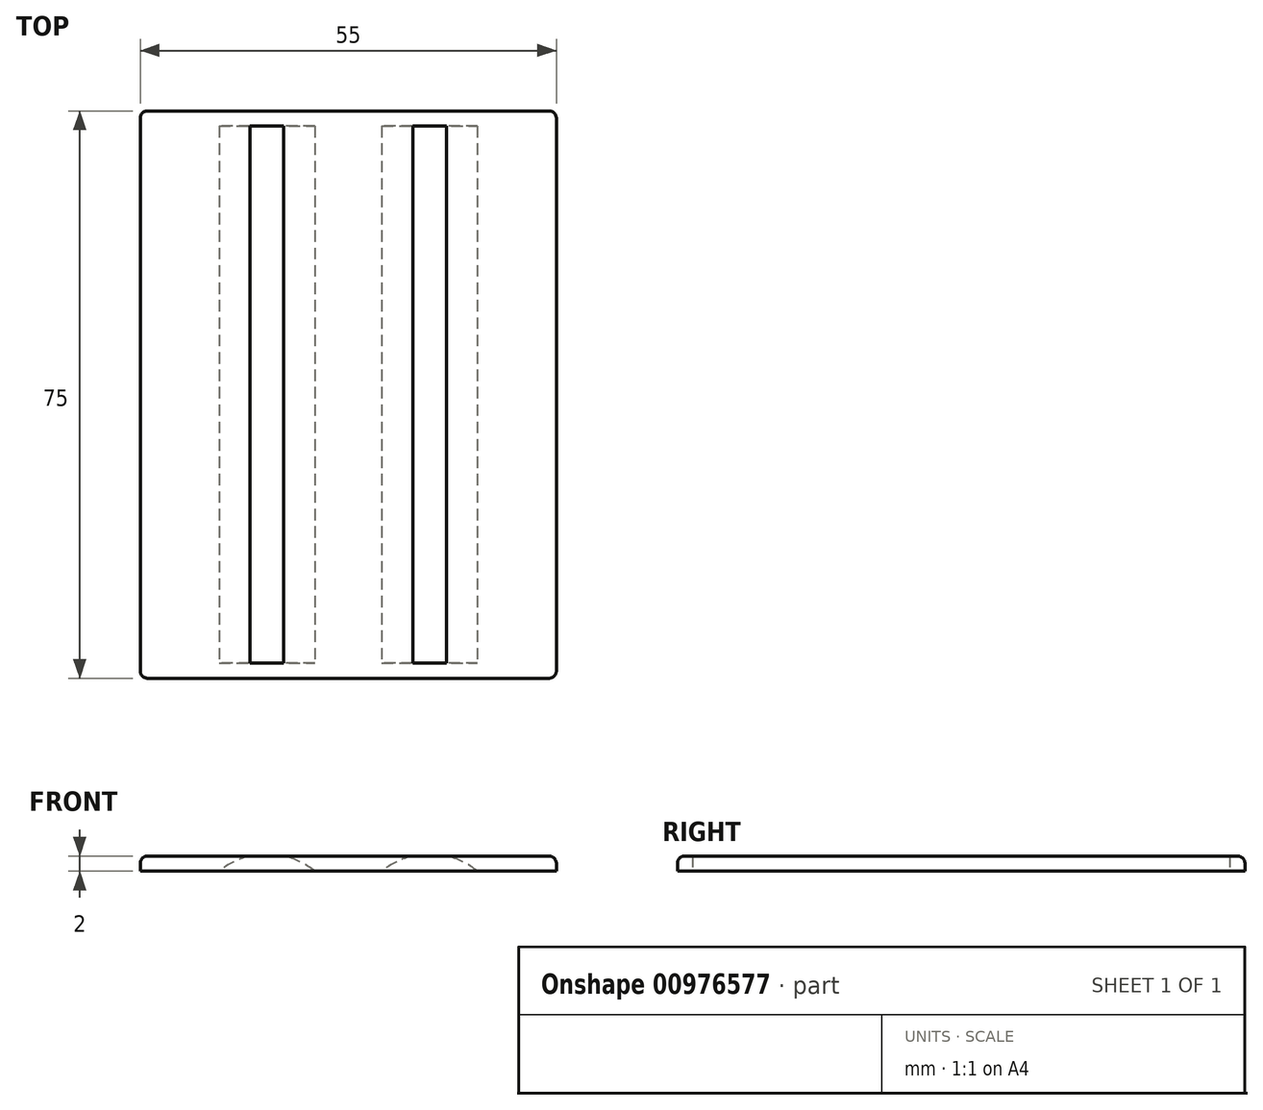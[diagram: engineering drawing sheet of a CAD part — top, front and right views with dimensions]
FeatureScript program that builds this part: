
annotation { "Feature Type Name" : "Feature", "Feature Type Description" : "" }
export const myFeature = defineFeature(function(context is Context, id is Id, definition is map)
    precondition{}
    {
        {
            var Q0;
            Q0=qCreatedBy(makeId("Top.planeOp"),FACE);
            var sketch = newSketch(context, id + "F0", { "sketchPlane" : qUnion([Q0])});
            skLineSegment(sketch, "E0.bottom", {"start": v(0, 0) * mm, "end": v(55, 0) * mm});
            skLineSegment(sketch, "E0.top", {"start": v(0, 73) * mm, "end": v(55, 73) * mm});
            skLineSegment(sketch, "E0.left", {"start": v(0, 0) * mm, "end": v(0, 73) * mm});
            skLineSegment(sketch, "E0.right", {"start": v(55, 0) * mm, "end": v(55, 73) * mm});
            skSolve(sketch);
        }
        {
            var Q0;
            Q0=makeQuery(id+"F0.imprint","IMPRINT",FACE,{"disambiguationData":[TD([[makeQuery(id+"F0.imprint","IMPRINT",EDGE,{"derivedFrom":sQuery(id+"F0.wireOp",EDGE,"E0.bottom")}),1.0]])]});
            extrude(context, id + "F1", {"entities" : qUnion([Q0]), "depth" : 2 * mm, "offsetDistance" : 25 * mm});
        }
        {
            var Q0;
            Q0=makeQuery(id+"F1.opExtrude","SWEPT_FACE",FACE,{"disambiguationData":[OSD([sQuery(id+"F0.wireOp",EDGE,"E0.bottom")])]});
            var sketch = newSketch(context, id + "F2", { "sketchPlane" : qUnion([Q0])});
            skCircle(sketch, "E1", {"center": v(16.75, -7.75) * mm, "radius": 10 * mm});
            skCircle(sketch, "E2", {"center": v(38.25, -7.75) * mm, "radius": 10 * mm});
            skSolve(sketch);
        }
        {
            var Q0;
            {var subQ0=sQuery(id+"F2.wireOp",EDGE,"E2");var subQ1=sQuery(id+"F0.wireOp",EDGE,"E0.bottom");var subQ2=makeQuery(id+"F1.opExtrude","CAP_EDGE",EDGE,{"disambiguationData":[OSD([subQ1])],"isStart":false});var subQ3=makeQuery(id+"F2.imprint","INTERSECT",VERTEX,{"disambiguationData":[OD(0.0)],"derivedFrom":[subQ2,subQ0]});Q0=makeQuery(id+"F2.imprint","IMPRINT",FACE,{"disambiguationData":[TD([[makeQuery(id+"F2.imprint","IMPRINT",EDGE,{"disambiguationData":[TD([[subQ3,1.0]])],"derivedFrom":subQ0}),1.0]])]});}
            var Q1;
            {var subQ0=sQuery(id+"F2.wireOp",EDGE,"E1");var subQ1=sQuery(id+"F0.wireOp",EDGE,"E0.bottom");var subQ2=makeQuery(id+"F1.opExtrude","CAP_EDGE",EDGE,{"disambiguationData":[OSD([subQ1])],"isStart":false});var subQ3=makeQuery(id+"F2.imprint","INTERSECT",VERTEX,{"disambiguationData":[OD(0.0)],"derivedFrom":[subQ2,subQ0]});Q1=makeQuery(id+"F2.imprint","IMPRINT",FACE,{"disambiguationData":[TD([[makeQuery(id+"F2.imprint","IMPRINT",EDGE,{"disambiguationData":[TD([[subQ3,1.0]])],"derivedFrom":subQ0}),1.0]])]});}
            extrude(context, id + "F3", {"entities" : qUnion([Q0, Q1]), "operationType" : NewBodyOperationType.REMOVE, "oppositeDirection" : true, "depth" : 71 * mm, "offsetDistance" : 25 * mm});
        }
        {
            var Q0;
            Q0=makeQuery(id+"F1.opExtrude","CAP_FACE",FACE,{"disambiguationData":[OSD([sQuery(id+"F0.wireOp",EDGE,"E0.bottom"),sQuery(id+"F0.wireOp",EDGE,"E0.top"),sQuery(id+"F0.wireOp",EDGE,"E0.left"),sQuery(id+"F0.wireOp",EDGE,"E0.right")])],"isStart":false});
            var sketch = newSketch(context, id + "F4", { "sketchPlane" : qUnion([Q0])});
            skLineSegment(sketch, "E3.bottom", {"start": v(55, 0) * mm, "end": v(0, 0) * mm});
            skLineSegment(sketch, "E3.top", {"start": v(55, -2) * mm, "end": v(0, -2) * mm});
            skLineSegment(sketch, "E3.left", {"start": v(55, 0) * mm, "end": v(55, -2) * mm});
            skLineSegment(sketch, "E3.right", {"start": v(0, 0) * mm, "end": v(0, -2) * mm});
            skSolve(sketch);
        }
        {
            var Q0;
            Q0=makeQuery(id+"F4.imprint","IMPRINT",FACE,{"disambiguationData":[TD([[makeQuery(id+"F4.imprint","IMPRINT",EDGE,{"derivedFrom":sQuery(id+"F4.wireOp",EDGE,"E3.top")}),-1.0]])]});
            extrude(context, id + "F5", {"entities" : qUnion([Q0]), "operationType" : NewBodyOperationType.ADD, "oppositeDirection" : true, "depth" : 2 * mm, "offsetDistance" : 25 * mm});
        }
        {
            var Q0;
            Q0=makeQuery(id+"F5.boolean.opBoolean","MERGE",EDGE,{"derivedFrom":[makeQuery(id+"F1.opExtrude","CAP_EDGE",EDGE,{"disambiguationData":[OSD([sQuery(id+"F0.wireOp",EDGE,"E0.left")])],"isStart":false}),makeQuery(id+"F5.opExtrude","CAP_EDGE",EDGE,{"disambiguationData":[OSD([sQuery(id+"F4.wireOp",EDGE,"E3.right")])],"isStart":true})]});
            var Q1;
            Q1=makeQuery(id+"F1.opExtrude","CAP_EDGE",EDGE,{"disambiguationData":[OSD([sQuery(id+"F0.wireOp",EDGE,"E0.top")])],"isStart":false});
            var Q2;
            Q2=makeQuery(id+"F5.boolean.opBoolean","MERGE",EDGE,{"derivedFrom":[makeQuery(id+"F1.opExtrude","CAP_EDGE",EDGE,{"disambiguationData":[OSD([sQuery(id+"F0.wireOp",EDGE,"E0.right")])],"isStart":false}),makeQuery(id+"F5.opExtrude","CAP_EDGE",EDGE,{"disambiguationData":[OSD([sQuery(id+"F4.wireOp",EDGE,"E3.left")])],"isStart":true})]});
            var Q3;
            Q3=makeQuery(id+"F5.opExtrude","CAP_EDGE",EDGE,{"disambiguationData":[OSD([sQuery(id+"F4.wireOp",EDGE,"E3.top")])],"isStart":true});
            var Q4;
            Q4=makeQuery(id+"F1.opExtrude","SWEPT_EDGE",EDGE,{"disambiguationData":[OSD([sQuery(id+"F0.wireOp",EDGE,"E0.top"),sQuery(id+"F0.wireOp",EDGE,"E0.right")])]});
            var Q5;
            Q5=makeQuery(id+"F1.opExtrude","SWEPT_EDGE",EDGE,{"disambiguationData":[OSD([sQuery(id+"F0.wireOp",EDGE,"E0.top"),sQuery(id+"F0.wireOp",EDGE,"E0.left")])]});
            var Q6;
            Q6=makeQuery(id+"F5.opExtrude","SWEPT_EDGE",EDGE,{"disambiguationData":[OSD([sQuery(id+"F4.wireOp",EDGE,"E3.top"),sQuery(id+"F4.wireOp",EDGE,"E3.right")])]});
            var Q7;
            Q7=makeQuery(id+"F5.opExtrude","SWEPT_EDGE",EDGE,{"disambiguationData":[OSD([sQuery(id+"F4.wireOp",EDGE,"E3.top"),sQuery(id+"F4.wireOp",EDGE,"E3.left")])]});
            fillet(context, id + "F6", {"entities" : qUnion([Q0, Q1, Q2, Q3, Q4, Q5, Q6, Q7]), "radius" : 1 * mm, "tangentPropagation" : true, "allowEdgeOverflow" : false});
        }
    });
